# Revit family: 879-002X7X-001-DN65-150
name_source: partatom
category: Pipe Accessories
units: mm (PartAtom-declared; Revit-internal decimal feet)

## family parameters
Always vertical = Yes
Cut with Voids When Loaded = No
Part Type = Valve - Breaks Into
Round Connector Dimension = Use Diameter
Shared = No
Work Plane-Based = No

## types (32) — shared parameters
879-0065-00-14400207299 = DN65_PN10/16
879-0065-00-144002072A0 = DN65_PN10/16
879-0065-00-14400217299 = DN65_PN10/16
879-0065-00-144002172A0 = DN65_PN10/16
879-0065-00-14400227299 = DN65_PN10/16
879-0065-00-144002272A0 = DN65_PN10/16
879-0080-00-14400207299 = DN80_PN10/16
879-0080-00-144002072A0 = DN80_PN10/16
879-0080-00-14400217299 = DN80_PN10/16
879-0080-00-144002172A0 = DN80_PN10/16
879-0080-00-14400227299 = DN80_PN10/16
879-0080-00-144002272A0 = DN80_PN10/16
879-0100-00-14400207299 = DN100_PN10/16
879-0100-00-144002072A0 = DN100_PN10/16
879-0100-00-14400217299 = DN100_PN10/16
879-0100-00-144002172A0 = DN100_PN10/16
879-0100-00-14400227299 = DN100_PN10/16
879-0100-00-144002272A0 = DN100_PN10/16
879-0125-00-14400207299 = DN125_PN10/16
879-0125-00-144002072A0 = DN125_PN10/16
879-0125-00-14400217299 = DN125_PN10/16
879-0125-00-144002172A0 = DN125_PN10/16
879-0125-00-14400227299 = DN125_PN10/16
879-0125-00-144002272A0 = DN125_PN10/16
879-0150-00-14400207299 = DN150_PN10/16
879-0150-00-144002072A0 = DN150_PN10/16
879-0150-00-14400217299 = DN150_PN10/16
879-0150-00-144002172A0 = DN150_PN10/16
879-0150-00-14400227299 = DN150_PN10/16
879-0150-00-144002272A0 = DN150_PN10/16
879-0150-00-14400237299 = DN150_PN10/16
879-0150-00-144002372A0 = DN150_PN10/16
Body_wall_thickness = 10 mm  [stored 0.0328084 ft]
Description_ = AVK CONST. FLOW/PRESS. RED. CONTROL VALVE
Flange_thickness = 19 mm
Search_Table = 879-002X7X-001-DN65-150
URL product pages = https://www.avkvalves.com

## per-type parameters (varying)
- 879-0065-00-14400207299_DN65_PN10/16: A=121.75 mm; Body_Collar_Dia=30.21 mm; Body_Collar_Dia_2=14.5 mm; Body_Flange_Dia=76.32 mm; Body_Flange_Dia_2=78.38 mm; Body_Height_1=72.5 mm; Body_Height_2=36.25 mm; Body_Height_3=58 mm; Body_Height_4=51.25 mm; Body_Top_Dia=9.06 mm; Body_Top_Dia_2=7.55 mm; Body_With_Dia=64.44 mm; Body_With_Dia_2=64.44 mm; Bolt_support=170.59 mm; Bolt_support_2=85.29 mm; Bolt_support_Dia=12 mm  [stored 0.0393701 ft]; Bolt_support_lenght=52.5 mm; Bolt_support_lenght_2=62.5 mm; Bottom_profile=16.25 mm  [stored 0.0533136 ft]; D1=59 mm; DN=65 mm; FOD=92.5 mm; Fillet_Length=6 mm  [stored 0.019685 ft]; H3=485 mm; ID=32.5 mm; L=290 mm; L1=307 mm; L_Ref=298.5 mm; L_ref_2=126 mm; PG_Dia=40 mm; PG_Ref=48.33 mm; PG_depth=8.4 mm  [stored 0.0275591 ft]; PG_ref=42.5 mm; Pilot_Dia_1=17.5 mm  [stored 0.0574147 ft]; Pilot_Dia_1_Ref=21 mm; Pilot_Dia_1_Ref_2=42 mm; Pilot_Dia_2=43.75 mm; Pilot_Dia_3=11.67 mm; Pilot_Dia_4=5.83 mm; Pilot_Dia_5=3.89 mm; Pilot_top_1=297.13 mm; Pilot_top_ref=95.38 mm; Profile1_Height=152 mm; Profile1_Length=25 mm; Profile1_Length_2=16.67 mm; Profile_Dia=6 mm  [stored 0.019685 ft]; Profile_Dia_2=6 mm  [stored 0.019685 ft]; Profile_Dia_3=12 mm  [stored 0.0393701 ft]; Top_Profile=102.35 mm; Top_Profile_Ref=107.35 mm; Top_Ref=201.75 mm; Top_Ref_2=249.44 mm; W=255 mm; W_Ref=211.25 mm
- 879-0065-00-144002072A0_DN65_PN10/16: A=121.75 mm; Body_Collar_Dia=30.21 mm; Body_Collar_Dia_2=14.5 mm; Body_Flange_Dia=76.32 mm; Body_Flange_Dia_2=78.38 mm; Body_Height_1=72.5 mm; Body_Height_2=36.25 mm; Body_Height_3=72.5 mm; Body_Height_4=51.25 mm; Body_Top_Dia=9.06 mm; Body_Top_Dia_2=7.55 mm; Body_With_Dia=64.44 mm; Body_With_Dia_2=64.44 mm; Bolt_support=170.59 mm; Bolt_support_2=85.29 mm; Bolt_support_Dia=12 mm  [stored 0.0393701 ft]; Bolt_support_lenght=52.55 mm; Bolt_support_lenght_2=62.55 mm; Bottom_profile=16.28 mm; D1=59 mm; DN=65.1 mm; FOD=92.5 mm; Fillet_Length=6 mm  [stored 0.019685 ft]; H3=485 mm; ID=32.55 mm; L=290 mm; L1=307 mm; L_Ref=298.5 mm; L_ref_2=126 mm; PG_Dia=40 mm; PG_Ref=48.33 mm; PG_depth=8.4 mm  [stored 0.0275591 ft]; PG_ref=42.55 mm; Pilot_Dia_1=17.5 mm  [stored 0.0574147 ft]; Pilot_Dia_1_Ref=21 mm; Pilot_Dia_1_Ref_2=42 mm; Pilot_Dia_2=43.75 mm; Pilot_Dia_3=11.67 mm; Pilot_Dia_4=5.83 mm; Pilot_Dia_5=3.89 mm; Pilot_top_1=304.38 mm; Pilot_top_ref=88.13 mm; Profile1_Height=170 mm; Profile1_Length=25 mm; Profile1_Length_2=16.67 mm; Profile_Dia=6 mm  [stored 0.019685 ft]; Profile_Dia_2=6 mm  [stored 0.019685 ft]; Profile_Dia_3=12 mm  [stored 0.0393701 ft]; Top_Profile=102.35 mm; Top_Profile_Ref=107.35 mm; Top_Ref=216.25 mm; Top_Ref_2=260.31 mm; W=255 mm; W_Ref=211.25 mm
- 879-0065-00-14400217299_DN65_PN10/16: A=121.75 mm; Body_Collar_Dia=30.21 mm; Body_Collar_Dia_2=14.5 mm; Body_Flange_Dia=76.32 mm; Body_Flange_Dia_2=78.38 mm; Body_Height_1=72.5 mm; Body_Height_2=36.25 mm; Body_Height_3=58 mm; Body_Height_4=51.25 mm; Body_Top_Dia=9.06 mm; Body_Top_Dia_2=7.55 mm; Body_With_Dia=64.44 mm; Body_With_Dia_2=64.44 mm; Bolt_support=170.59 mm; Bolt_support_2=85.29 mm; Bolt_support_Dia=12 mm  [stored 0.0393701 ft]; Bolt_support_lenght=52.6 mm; Bolt_support_lenght_2=62.6 mm; Bottom_profile=16.3 mm; D1=59 mm; DN=65.2 mm; FOD=92.5 mm; Fillet_Length=6 mm  [stored 0.019685 ft]; H3=485 mm; ID=32.6 mm; L=290 mm; L1=307 mm; L_Ref=298.5 mm; L_ref_2=126 mm; PG_Dia=40 mm; PG_Ref=48.33 mm; PG_depth=8.4 mm  [stored 0.0275591 ft]; PG_ref=42.6 mm; Pilot_Dia_1=17.5 mm  [stored 0.0574147 ft]; Pilot_Dia_1_Ref=21 mm; Pilot_Dia_1_Ref_2=42 mm; Pilot_Dia_2=43.75 mm; Pilot_Dia_3=11.67 mm; Pilot_Dia_4=5.83 mm; Pilot_Dia_5=3.89 mm; Pilot_top_1=297.13 mm; Pilot_top_ref=95.38 mm; Profile1_Height=152 mm; Profile1_Length=25 mm; Profile1_Length_2=16.67 mm; Profile_Dia=6 mm  [stored 0.019685 ft]; Profile_Dia_2=6 mm  [stored 0.019685 ft]; Profile_Dia_3=12 mm  [stored 0.0393701 ft]; Top_Profile=102.35 mm; Top_Profile_Ref=107.35 mm; Top_Ref=201.75 mm; Top_Ref_2=249.44 mm; W=255 mm; W_Ref=211.25 mm
- 879-0065-00-144002172A0_DN65_PN10/16: A=121.75 mm; Body_Collar_Dia=30.21 mm; Body_Collar_Dia_2=14.5 mm; Body_Flange_Dia=76.32 mm; Body_Flange_Dia_2=78.38 mm; Body_Height_1=72.5 mm; Body_Height_2=36.25 mm; Body_Height_3=72.5 mm; Body_Height_4=51.25 mm; Body_Top_Dia=9.06 mm; Body_Top_Dia_2=7.55 mm; Body_With_Dia=64.44 mm; Body_With_Dia_2=64.44 mm; Bolt_support=170.59 mm; Bolt_support_2=85.29 mm; Bolt_support_Dia=12 mm  [stored 0.0393701 ft]; Bolt_support_lenght=52.65 mm; Bolt_support_lenght_2=62.65 mm; Bottom_profile=16.33 mm; D1=59 mm; DN=65.3 mm; FOD=92.5 mm; Fillet_Length=6 mm  [stored 0.019685 ft]; H3=485 mm; ID=32.65 mm; L=290 mm; L1=307 mm; L_Ref=298.5 mm; L_ref_2=126 mm; PG_Dia=40 mm; PG_Ref=48.33 mm; PG_depth=8.4 mm  [stored 0.0275591 ft]; PG_ref=42.65 mm; Pilot_Dia_1=17.5 mm  [stored 0.0574147 ft]; Pilot_Dia_1_Ref=21 mm; Pilot_Dia_1_Ref_2=42 mm; Pilot_Dia_2=43.75 mm; Pilot_Dia_3=11.67 mm; Pilot_Dia_4=5.83 mm; Pilot_Dia_5=3.89 mm; Pilot_top_1=304.38 mm; Pilot_top_ref=88.13 mm; Profile1_Height=170 mm; Profile1_Length=25 mm; Profile1_Length_2=16.67 mm; Profile_Dia=6 mm  [stored 0.019685 ft]; Profile_Dia_2=6 mm  [stored 0.019685 ft]; Profile_Dia_3=12 mm  [stored 0.0393701 ft]; Top_Profile=102.35 mm; Top_Profile_Ref=107.35 mm; Top_Ref=216.25 mm; Top_Ref_2=260.31 mm; W=255 mm; W_Ref=211.25 mm
- 879-0065-00-14400227299_DN65_PN10/16: A=121.75 mm; Body_Collar_Dia=30.21 mm; Body_Collar_Dia_2=14.5 mm; Body_Flange_Dia=76.32 mm; Body_Flange_Dia_2=78.38 mm; Body_Height_1=72.5 mm; Body_Height_2=36.25 mm; Body_Height_3=58 mm; Body_Height_4=51.25 mm; Body_Top_Dia=9.06 mm; Body_Top_Dia_2=7.55 mm; Body_With_Dia=64.44 mm; Body_With_Dia_2=64.44 mm; Bolt_support=170.59 mm; Bolt_support_2=85.29 mm; Bolt_support_Dia=12 mm  [stored 0.0393701 ft]; Bolt_support_lenght=52.7 mm; Bolt_support_lenght_2=62.7 mm; Bottom_profile=16.35 mm  [stored 0.0536417 ft]; D1=59 mm; DN=65.4 mm; FOD=92.5 mm; Fillet_Length=6 mm  [stored 0.019685 ft]; H3=485 mm; ID=32.7 mm; L=290 mm; L1=307 mm; L_Ref=298.5 mm; L_ref_2=126 mm; PG_Dia=40 mm; PG_Ref=48.33 mm; PG_depth=8.4 mm  [stored 0.0275591 ft]; PG_ref=42.7 mm; Pilot_Dia_1=17.5 mm  [stored 0.0574147 ft]; Pilot_Dia_1_Ref=21 mm; Pilot_Dia_1_Ref_2=42 mm; Pilot_Dia_2=43.75 mm; Pilot_Dia_3=11.67 mm; Pilot_Dia_4=5.83 mm; Pilot_Dia_5=3.89 mm; Pilot_top_1=297.13 mm; Pilot_top_ref=95.38 mm; Profile1_Height=152 mm; Profile1_Length=25 mm; Profile1_Length_2=16.67 mm; Profile_Dia=6 mm  [stored 0.019685 ft]; Profile_Dia_2=6 mm  [stored 0.019685 ft]; Profile_Dia_3=12 mm  [stored 0.0393701 ft]; Top_Profile=102.35 mm; Top_Profile_Ref=107.35 mm; Top_Ref=201.75 mm; Top_Ref_2=249.44 mm; W=255 mm; W_Ref=211.25 mm
- 879-0065-00-144002272A0_DN65_PN10/16: A=121.75 mm; Body_Collar_Dia=30.21 mm; Body_Collar_Dia_2=14.5 mm; Body_Flange_Dia=76.32 mm; Body_Flange_Dia_2=78.38 mm; Body_Height_1=72.5 mm; Body_Height_2=36.25 mm; Body_Height_3=72.5 mm; Body_Height_4=51.25 mm; Body_Top_Dia=9.06 mm; Body_Top_Dia_2=7.55 mm; Body_With_Dia=64.44 mm; Body_With_Dia_2=64.44 mm; Bolt_support=170.59 mm; Bolt_support_2=85.29 mm; Bolt_support_Dia=12 mm  [stored 0.0393701 ft]; Bolt_support_lenght=52.75 mm; Bolt_support_lenght_2=62.75 mm; Bottom_profile=16.38 mm; D1=59 mm; DN=65.5 mm; FOD=92.5 mm; Fillet_Length=6 mm  [stored 0.019685 ft]; H3=485 mm; ID=32.75 mm; L=290 mm; L1=307 mm; L_Ref=298.5 mm; L_ref_2=126 mm; PG_Dia=40 mm; PG_Ref=48.33 mm; PG_depth=8.4 mm  [stored 0.0275591 ft]; PG_ref=42.75 mm; Pilot_Dia_1=17.5 mm  [stored 0.0574147 ft]; Pilot_Dia_1_Ref=21 mm; Pilot_Dia_1_Ref_2=42 mm; Pilot_Dia_2=43.75 mm; Pilot_Dia_3=11.67 mm; Pilot_Dia_4=5.83 mm; Pilot_Dia_5=3.89 mm; Pilot_top_1=304.38 mm; Pilot_top_ref=88.13 mm; Profile1_Height=170 mm; Profile1_Length=25 mm; Profile1_Length_2=16.67 mm; Profile_Dia=6 mm  [stored 0.019685 ft]; Profile_Dia_2=6 mm  [stored 0.019685 ft]; Profile_Dia_3=12 mm  [stored 0.0393701 ft]; Top_Profile=102.35 mm; Top_Profile_Ref=107.35 mm; Top_Ref=216.25 mm; Top_Ref_2=260.31 mm; W=255 mm; W_Ref=211.25 mm
- 879-0100-00-14400207299_DN100_PN10/16: A=128 mm; Body_Collar_Dia=36.46 mm; Body_Collar_Dia_2=17.5 mm  [stored 0.0574147 ft]; Body_Flange_Dia=92.11 mm; Body_Flange_Dia_2=94.59 mm; Body_Height_1=87.5 mm; Body_Height_2=43.75 mm; Body_Height_3=58.5 mm; Body_Height_4=58.75 mm; Body_Top_Dia=10.94 mm; Body_Top_Dia_2=9.11 mm; Body_With_Dia=77.78 mm; Body_With_Dia_2=77.78 mm; Bolt_support=205.88 mm; Bolt_support_2=102.94 mm; Bolt_support_Dia=12 mm  [stored 0.0393701 ft]; Bolt_support_lenght=70 mm; Bolt_support_lenght_2=80 mm; Bottom_profile=25 mm; D1=78 mm; DN=100 mm; FOD=110 mm; Fillet_Length=6 mm  [stored 0.019685 ft]; H3=520 mm; ID=50 mm; L=350 mm; L1=367 mm; L_Ref=358.5 mm; L_ref_2=156 mm; PG_Dia=40 mm; PG_Ref=58.33 mm; PG_depth=8.4 mm  [stored 0.0275591 ft]; PG_ref=60 mm; Pilot_Dia_1=22 mm; Pilot_Dia_1_Ref=26.4 mm; Pilot_Dia_1_Ref_2=52.8 mm; Pilot_Dia_2=55 mm; Pilot_Dia_3=14.67 mm; Pilot_Dia_4=7.33 mm; Pilot_Dia_5=4.89 mm; Pilot_top_1=317.38 mm; Pilot_top_ref=92.63 mm; Profile1_Height=185 mm; Profile1_Length=29.73 mm; Profile1_Length_2=19.82 mm; Profile_Dia=6 mm  [stored 0.019685 ft]; Profile_Dia_2=6 mm  [stored 0.019685 ft]; Profile_Dia_3=12 mm  [stored 0.0393701 ft]; Top_Profile=123.53 mm; Top_Profile_Ref=128.53 mm; Top_Ref=224.75 mm; Top_Ref_2=271.06 mm; W=290 mm; W_Ref=235 mm
- 879-0100-00-144002072A0_DN100_PN10/16: A=128 mm; Body_Collar_Dia=36.46 mm; Body_Collar_Dia_2=17.5 mm  [stored 0.0574147 ft]; Body_Flange_Dia=92.11 mm; Body_Flange_Dia_2=94.59 mm; Body_Height_1=87.5 mm; Body_Height_2=43.75 mm; Body_Height_3=70 mm; Body_Height_4=58.75 mm; Body_Top_Dia=10.94 mm; Body_Top_Dia_2=9.11 mm; Body_With_Dia=77.78 mm; Body_With_Dia_2=77.78 mm; Bolt_support=205.88 mm; Bolt_support_2=102.94 mm; Bolt_support_Dia=12 mm  [stored 0.0393701 ft]; Bolt_support_lenght=70.05 mm; Bolt_support_lenght_2=80.05 mm; Bottom_profile=25.03 mm; D1=78 mm; DN=100.1 mm; FOD=110 mm; Fillet_Length=6 mm  [stored 0.019685 ft]; H3=520 mm; ID=50.05 mm; L=350 mm; L1=367 mm; L_Ref=358.5 mm; L_ref_2=156 mm; PG_Dia=40 mm; PG_Ref=58.33 mm; PG_depth=8.4 mm  [stored 0.0275591 ft]; PG_ref=60.05 mm; Pilot_Dia_1=22 mm; Pilot_Dia_1_Ref=26.4 mm; Pilot_Dia_1_Ref_2=52.8 mm; Pilot_Dia_2=55 mm; Pilot_Dia_3=14.67 mm; Pilot_Dia_4=7.33 mm; Pilot_Dia_5=4.89 mm; Pilot_top_1=323.13 mm; Pilot_top_ref=86.88 mm; Profile1_Height=176 mm; Profile1_Length=29.73 mm; Profile1_Length_2=19.82 mm; Profile_Dia=6 mm  [stored 0.019685 ft]; Profile_Dia_2=6 mm  [stored 0.019685 ft]; Profile_Dia_3=12 mm  [stored 0.0393701 ft]; Top_Profile=123.53 mm; Top_Profile_Ref=128.53 mm; Top_Ref=236.25 mm; Top_Ref_2=279.69 mm; W=290 mm; W_Ref=235 mm
- 879-0100-00-14400217299_DN100_PN10/16: A=128 mm; Body_Collar_Dia=36.46 mm; Body_Collar_Dia_2=17.5 mm  [stored 0.0574147 ft]; Body_Flange_Dia=92.11 mm; Body_Flange_Dia_2=94.59 mm; Body_Height_1=87.5 mm; Body_Height_2=43.75 mm; Body_Height_3=58.5 mm; Body_Height_4=58.75 mm; Body_Top_Dia=10.94 mm; Body_Top_Dia_2=9.11 mm; Body_With_Dia=77.78 mm; Body_With_Dia_2=77.78 mm; Bolt_support=205.88 mm; Bolt_support_2=102.94 mm; Bolt_support_Dia=12 mm  [stored 0.0393701 ft]; Bolt_support_lenght=70.1 mm; Bolt_support_lenght_2=80.1 mm; Bottom_profile=25.05 mm; D1=78 mm; DN=100.2 mm; FOD=110 mm; Fillet_Length=6 mm  [stored 0.019685 ft]; H3=520 mm; ID=50.1 mm; L=350 mm; L1=367 mm; L_Ref=358.5 mm; L_ref_2=156 mm; PG_Dia=40 mm; PG_Ref=58.33 mm; PG_depth=8.4 mm  [stored 0.0275591 ft]; PG_ref=60.1 mm; Pilot_Dia_1=22 mm; Pilot_Dia_1_Ref=26.4 mm; Pilot_Dia_1_Ref_2=52.8 mm; Pilot_Dia_2=55 mm; Pilot_Dia_3=14.67 mm; Pilot_Dia_4=7.33 mm; Pilot_Dia_5=4.89 mm; Pilot_top_1=317.38 mm; Pilot_top_ref=92.63 mm; Profile1_Height=185 mm; Profile1_Length=29.73 mm; Profile1_Length_2=19.82 mm; Profile_Dia=6 mm  [stored 0.019685 ft]; Profile_Dia_2=6 mm  [stored 0.019685 ft]; Profile_Dia_3=12 mm  [stored 0.0393701 ft]; Top_Profile=123.53 mm; Top_Profile_Ref=128.53 mm; Top_Ref=224.75 mm; Top_Ref_2=271.06 mm; W=290 mm; W_Ref=235 mm
- 879-0100-00-144002172A0_DN100_PN10/16: A=128 mm; Body_Collar_Dia=36.46 mm; Body_Collar_Dia_2=17.5 mm  [stored 0.0574147 ft]; Body_Flange_Dia=92.11 mm; Body_Flange_Dia_2=94.59 mm; Body_Height_1=87.5 mm; Body_Height_2=43.75 mm; Body_Height_3=70 mm; Body_Height_4=58.75 mm; Body_Top_Dia=10.94 mm; Body_Top_Dia_2=9.11 mm; Body_With_Dia=77.78 mm; Body_With_Dia_2=77.78 mm; Bolt_support=205.88 mm; Bolt_support_2=102.94 mm; Bolt_support_Dia=12 mm  [stored 0.0393701 ft]; Bolt_support_lenght=70.15 mm; Bolt_support_lenght_2=80.15 mm; Bottom_profile=25.08 mm; D1=78 mm; DN=100.3 mm; FOD=110 mm; Fillet_Length=6 mm  [stored 0.019685 ft]; H3=520 mm; ID=50.15 mm; L=350 mm; L1=367 mm; L_Ref=358.5 mm; L_ref_2=156 mm; PG_Dia=40 mm; PG_Ref=58.33 mm; PG_depth=8.4 mm  [stored 0.0275591 ft]; PG_ref=60.15 mm; Pilot_Dia_1=22 mm; Pilot_Dia_1_Ref=26.4 mm; Pilot_Dia_1_Ref_2=52.8 mm; Pilot_Dia_2=55 mm; Pilot_Dia_3=14.67 mm; Pilot_Dia_4=7.33 mm; Pilot_Dia_5=4.89 mm; Pilot_top_1=323.13 mm; Pilot_top_ref=86.88 mm; Profile1_Height=176 mm; Profile1_Length=29.73 mm; Profile1_Length_2=19.82 mm; Profile_Dia=6 mm  [stored 0.019685 ft]; Profile_Dia_2=6 mm  [stored 0.019685 ft]; Profile_Dia_3=12 mm  [stored 0.0393701 ft]; Top_Profile=123.53 mm; Top_Profile_Ref=128.53 mm; Top_Ref=236.25 mm; Top_Ref_2=279.69 mm; W=290 mm; W_Ref=235 mm
- 879-0100-00-14400227299_DN100_PN10/16: A=128 mm; Body_Collar_Dia=36.46 mm; Body_Collar_Dia_2=17.5 mm  [stored 0.0574147 ft]; Body_Flange_Dia=92.11 mm; Body_Flange_Dia_2=94.59 mm; Body_Height_1=87.5 mm; Body_Height_2=43.75 mm; Body_Height_3=58.5 mm; Body_Height_4=58.75 mm; Body_Top_Dia=10.94 mm; Body_Top_Dia_2=9.11 mm; Body_With_Dia=77.78 mm; Body_With_Dia_2=77.78 mm; Bolt_support=205.88 mm; Bolt_support_2=102.94 mm; Bolt_support_Dia=12 mm  [stored 0.0393701 ft]; Bolt_support_lenght=70.2 mm; Bolt_support_lenght_2=80.2 mm; Bottom_profile=25.1 mm; D1=78 mm; DN=100.4 mm; FOD=110 mm; Fillet_Length=6 mm  [stored 0.019685 ft]; H3=520 mm; ID=50.2 mm; L=350 mm; L1=367 mm; L_Ref=358.5 mm; L_ref_2=156 mm; PG_Dia=40 mm; PG_Ref=58.33 mm; PG_depth=8.4 mm  [stored 0.0275591 ft]; PG_ref=60.2 mm; Pilot_Dia_1=22 mm; Pilot_Dia_1_Ref=26.4 mm; Pilot_Dia_1_Ref_2=52.8 mm; Pilot_Dia_2=55 mm; Pilot_Dia_3=14.67 mm; Pilot_Dia_4=7.33 mm; Pilot_Dia_5=4.89 mm; Pilot_top_1=317.38 mm; Pilot_top_ref=92.63 mm; Profile1_Height=185 mm; Profile1_Length=29.73 mm; Profile1_Length_2=19.82 mm; Profile_Dia=6 mm  [stored 0.019685 ft]; Profile_Dia_2=6 mm  [stored 0.019685 ft]; Profile_Dia_3=12 mm  [stored 0.0393701 ft]; Top_Profile=123.53 mm; Top_Profile_Ref=128.53 mm; Top_Ref=224.75 mm; Top_Ref_2=271.06 mm; W=290 mm; W_Ref=235 mm
- 879-0100-00-144002272A0_DN100_PN10/16: A=128 mm; Body_Collar_Dia=36.46 mm; Body_Collar_Dia_2=17.5 mm  [stored 0.0574147 ft]; Body_Flange_Dia=92.11 mm; Body_Flange_Dia_2=94.59 mm; Body_Height_1=87.5 mm; Body_Height_2=43.75 mm; Body_Height_3=70 mm; Body_Height_4=58.75 mm; Body_Top_Dia=10.94 mm; Body_Top_Dia_2=9.11 mm; Body_With_Dia=77.78 mm; Body_With_Dia_2=77.78 mm; Bolt_support=205.88 mm; Bolt_support_2=102.94 mm; Bolt_support_Dia=12 mm  [stored 0.0393701 ft]; Bolt_support_lenght=70.25 mm; Bolt_support_lenght_2=80.25 mm; Bottom_profile=25.13 mm; D1=78 mm; DN=100.5 mm; FOD=110 mm; Fillet_Length=6 mm  [stored 0.019685 ft]; H3=520 mm; ID=50.25 mm; L=350 mm; L1=367 mm; L_Ref=358.5 mm; L_ref_2=156 mm; PG_Dia=40 mm; PG_Ref=58.33 mm; PG_depth=8.4 mm  [stored 0.0275591 ft]; PG_ref=60.25 mm; Pilot_Dia_1=22 mm; Pilot_Dia_1_Ref=26.4 mm; Pilot_Dia_1_Ref_2=52.8 mm; Pilot_Dia_2=55 mm; Pilot_Dia_3=14.67 mm; Pilot_Dia_4=7.33 mm; Pilot_Dia_5=4.89 mm; Pilot_top_1=323.13 mm; Pilot_top_ref=86.88 mm; Profile1_Height=176 mm; Profile1_Length=29.73 mm; Profile1_Length_2=19.82 mm; Profile_Dia=6 mm  [stored 0.019685 ft]; Profile_Dia_2=6 mm  [stored 0.019685 ft]; Profile_Dia_3=12 mm  [stored 0.0393701 ft]; Top_Profile=123.53 mm; Top_Profile_Ref=128.53 mm; Top_Ref=236.25 mm; Top_Ref_2=279.69 mm; W=290 mm; W_Ref=235 mm
- 879-0125-00-14400207299_DN125_PN10/16: A=119.25 mm; Body_Collar_Dia=41.67 mm; Body_Collar_Dia_2=20 mm; Body_Flange_Dia=105.26 mm; Body_Flange_Dia_2=108.11 mm; Body_Height_1=100 mm; Body_Height_2=50 mm; Body_Height_3=58.5 mm; Body_Height_4=65 mm; Body_Top_Dia=12.5 mm  [stored 0.0410105 ft]; Body_Top_Dia_2=10.42 mm; Body_With_Dia=88.89 mm; Body_With_Dia_2=88.89 mm; Bolt_support=235.29 mm; Bolt_support_2=117.65 mm; Bolt_support_Dia=12 mm  [stored 0.0393701 ft]; Bolt_support_lenght=82.5 mm; Bolt_support_lenght_2=92.5 mm; Bottom_profile=31.25 mm; D1=92 mm; DN=125 mm; FOD=125 mm; Fillet_Length=6 mm  [stored 0.019685 ft]; H3=540 mm; ID=62.5 mm; L=400 mm; L1=417 mm; L_Ref=408.5 mm; L_ref_2=181 mm; PG_Dia=40 mm; PG_Ref=66.67 mm; PG_depth=8.4 mm  [stored 0.0275591 ft]; PG_ref=72.5 mm; Pilot_Dia_1=27.5 mm; Pilot_Dia_1_Ref=33 mm; Pilot_Dia_1_Ref_2=66 mm; Pilot_Dia_2=68.75 mm; Pilot_Dia_3=18.33 mm; Pilot_Dia_4=9.17 mm; Pilot_Dia_5=6.11 mm; Pilot_top_1=329.25 mm; Pilot_top_ref=85.75 mm; Profile1_Height=205 mm; Profile1_Length=33.78 mm; Profile1_Length_2=22.52 mm; Profile_Dia=6 mm  [stored 0.019685 ft]; Profile_Dia_2=6 mm  [stored 0.019685 ft]; Profile_Dia_3=12 mm  [stored 0.0393701 ft]; Top_Profile=141.18 mm; Top_Profile_Ref=146.18 mm; Top_Ref=243.5 mm; Top_Ref_2=286.38 mm; W=310 mm; W_Ref=241.25 mm
- 879-0125-00-144002072A0_DN125_PN10/16: A=119.25 mm; Body_Collar_Dia=41.67 mm; Body_Collar_Dia_2=20 mm; Body_Flange_Dia=105.26 mm; Body_Flange_Dia_2=108.11 mm; Body_Height_1=100 mm; Body_Height_2=50 mm; Body_Height_3=70 mm; Body_Height_4=65 mm; Body_Top_Dia=12.5 mm  [stored 0.0410105 ft]; Body_Top_Dia_2=10.42 mm; Body_With_Dia=88.89 mm; Body_With_Dia_2=88.89 mm; Bolt_support=235.29 mm; Bolt_support_2=117.65 mm; Bolt_support_Dia=12 mm  [stored 0.0393701 ft]; Bolt_support_lenght=82.55 mm; Bolt_support_lenght_2=92.55 mm; Bottom_profile=31.28 mm; D1=92 mm; DN=125.1 mm; FOD=125 mm; Fillet_Length=6 mm  [stored 0.019685 ft]; H3=540 mm; ID=62.55 mm; L=400 mm; L1=417 mm; L_Ref=408.5 mm; L_ref_2=181 mm; PG_Dia=40 mm; PG_Ref=66.67 mm; PG_depth=8.4 mm  [stored 0.0275591 ft]; PG_ref=72.55 mm; Pilot_Dia_1=27.5 mm; Pilot_Dia_1_Ref=33 mm; Pilot_Dia_1_Ref_2=66 mm; Pilot_Dia_2=68.75 mm; Pilot_Dia_3=18.33 mm; Pilot_Dia_4=9.17 mm; Pilot_Dia_5=6.11 mm; Pilot_top_1=335 mm; Pilot_top_ref=80 mm; Profile1_Height=195 mm; Profile1_Length=33.78 mm; Profile1_Length_2=22.52 mm; Profile_Dia=6 mm  [stored 0.019685 ft]; Profile_Dia_2=6 mm  [stored 0.019685 ft]; Profile_Dia_3=12 mm  [stored 0.0393701 ft]; Top_Profile=141.18 mm; Top_Profile_Ref=146.18 mm; Top_Ref=255 mm; Top_Ref_2=295 mm; W=310 mm; W_Ref=241.25 mm
- 879-0125-00-14400217299_DN125_PN10/16: A=119.25 mm; Body_Collar_Dia=41.67 mm; Body_Collar_Dia_2=20 mm; Body_Flange_Dia=105.26 mm; Body_Flange_Dia_2=108.11 mm; Body_Height_1=100 mm; Body_Height_2=50 mm; Body_Height_3=58.5 mm; Body_Height_4=65 mm; Body_Top_Dia=12.5 mm  [stored 0.0410105 ft]; Body_Top_Dia_2=10.42 mm; Body_With_Dia=88.89 mm; Body_With_Dia_2=88.89 mm; Bolt_support=235.29 mm; Bolt_support_2=117.65 mm; Bolt_support_Dia=12 mm  [stored 0.0393701 ft]; Bolt_support_lenght=82.6 mm; Bolt_support_lenght_2=92.6 mm; Bottom_profile=31.3 mm; D1=92 mm; DN=125.2 mm; FOD=125 mm; Fillet_Length=6 mm  [stored 0.019685 ft]; H3=540 mm; ID=62.6 mm; L=400 mm; L1=417 mm; L_Ref=408.5 mm; L_ref_2=181 mm; PG_Dia=40 mm; PG_Ref=66.67 mm; PG_depth=8.4 mm  [stored 0.0275591 ft]; PG_ref=72.6 mm; Pilot_Dia_1=27.5 mm; Pilot_Dia_1_Ref=33 mm; Pilot_Dia_1_Ref_2=66 mm; Pilot_Dia_2=68.75 mm; Pilot_Dia_3=18.33 mm; Pilot_Dia_4=9.17 mm; Pilot_Dia_5=6.11 mm; Pilot_top_1=329.25 mm; Pilot_top_ref=85.75 mm; Profile1_Height=205 mm; Profile1_Length=33.78 mm; Profile1_Length_2=22.52 mm; Profile_Dia=6 mm  [stored 0.019685 ft]; Profile_Dia_2=6 mm  [stored 0.019685 ft]; Profile_Dia_3=12 mm  [stored 0.0393701 ft]; Top_Profile=141.18 mm; Top_Profile_Ref=146.18 mm; Top_Ref=243.5 mm; Top_Ref_2=286.38 mm; W=310 mm; W_Ref=241.25 mm
- 879-0125-00-144002172A0_DN125_PN10/16: A=119.25 mm; Body_Collar_Dia=41.67 mm; Body_Collar_Dia_2=20 mm; Body_Flange_Dia=105.26 mm; Body_Flange_Dia_2=108.11 mm; Body_Height_1=100 mm; Body_Height_2=50 mm; Body_Height_3=70 mm; Body_Height_4=65 mm; Body_Top_Dia=12.5 mm  [stored 0.0410105 ft]; Body_Top_Dia_2=10.42 mm; Body_With_Dia=88.89 mm; Body_With_Dia_2=88.89 mm; Bolt_support=235.29 mm; Bolt_support_2=117.65 mm; Bolt_support_Dia=12 mm  [stored 0.0393701 ft]; Bolt_support_lenght=82.65 mm; Bolt_support_lenght_2=92.65 mm; Bottom_profile=31.33 mm; D1=92 mm; DN=125.3 mm; FOD=125 mm; Fillet_Length=6 mm  [stored 0.019685 ft]; H3=540 mm; ID=62.65 mm; L=400 mm; L1=417 mm; L_Ref=408.5 mm; L_ref_2=181 mm; PG_Dia=40 mm; PG_Ref=66.67 mm; PG_depth=8.4 mm  [stored 0.0275591 ft]; PG_ref=72.65 mm; Pilot_Dia_1=27.5 mm; Pilot_Dia_1_Ref=33 mm; Pilot_Dia_1_Ref_2=66 mm; Pilot_Dia_2=68.75 mm; Pilot_Dia_3=18.33 mm; Pilot_Dia_4=9.17 mm; Pilot_Dia_5=6.11 mm; Pilot_top_1=335 mm; Pilot_top_ref=80 mm; Profile1_Height=195 mm; Profile1_Length=33.78 mm; Profile1_Length_2=22.52 mm; Profile_Dia=6 mm  [stored 0.019685 ft]; Profile_Dia_2=6 mm  [stored 0.019685 ft]; Profile_Dia_3=12 mm  [stored 0.0393701 ft]; Top_Profile=141.18 mm; Top_Profile_Ref=146.18 mm; Top_Ref=255 mm; Top_Ref_2=295 mm; W=310 mm; W_Ref=241.25 mm
- 879-0125-00-14400227299_DN125_PN10/16: A=119.25 mm; Body_Collar_Dia=41.67 mm; Body_Collar_Dia_2=20 mm; Body_Flange_Dia=105.26 mm; Body_Flange_Dia_2=108.11 mm; Body_Height_1=100 mm; Body_Height_2=50 mm; Body_Height_3=58.5 mm; Body_Height_4=65 mm; Body_Top_Dia=12.5 mm  [stored 0.0410105 ft]; Body_Top_Dia_2=10.42 mm; Body_With_Dia=88.89 mm; Body_With_Dia_2=88.89 mm; Bolt_support=235.29 mm; Bolt_support_2=117.65 mm; Bolt_support_Dia=12 mm  [stored 0.0393701 ft]; Bolt_support_lenght=82.7 mm; Bolt_support_lenght_2=92.7 mm; Bottom_profile=31.35 mm; D1=92 mm; DN=125.4 mm; FOD=125 mm; Fillet_Length=6 mm  [stored 0.019685 ft]; H3=540 mm; ID=62.7 mm; L=400 mm; L1=417 mm; L_Ref=408.5 mm; L_ref_2=181 mm; PG_Dia=40 mm; PG_Ref=66.67 mm; PG_depth=8.4 mm  [stored 0.0275591 ft]; PG_ref=72.7 mm; Pilot_Dia_1=27.5 mm; Pilot_Dia_1_Ref=33 mm; Pilot_Dia_1_Ref_2=66 mm; Pilot_Dia_2=68.75 mm; Pilot_Dia_3=18.33 mm; Pilot_Dia_4=9.17 mm; Pilot_Dia_5=6.11 mm; Pilot_top_1=329.25 mm; Pilot_top_ref=85.75 mm; Profile1_Height=205 mm; Profile1_Length=33.78 mm; Profile1_Length_2=22.52 mm; Profile_Dia=6 mm  [stored 0.019685 ft]; Profile_Dia_2=6 mm  [stored 0.019685 ft]; Profile_Dia_3=12 mm  [stored 0.0393701 ft]; Top_Profile=141.18 mm; Top_Profile_Ref=146.18 mm; Top_Ref=243.5 mm; Top_Ref_2=286.38 mm; W=310 mm; W_Ref=241.25 mm
- 879-0125-00-144002272A0_DN125_PN10/16: A=119.25 mm; Body_Collar_Dia=41.67 mm; Body_Collar_Dia_2=20 mm; Body_Flange_Dia=105.26 mm; Body_Flange_Dia_2=108.11 mm; Body_Height_1=100 mm; Body_Height_2=50 mm; Body_Height_3=70 mm; Body_Height_4=65 mm; Body_Top_Dia=12.5 mm  [stored 0.0410105 ft]; Body_Top_Dia_2=10.42 mm; Body_With_Dia=88.89 mm; Body_With_Dia_2=88.89 mm; Bolt_support=235.29 mm; Bolt_support_2=117.65 mm; Bolt_support_Dia=12 mm  [stored 0.0393701 ft]; Bolt_support_lenght=82.75 mm; Bolt_support_lenght_2=92.75 mm; Bottom_profile=31.38 mm; D1=92 mm; DN=125.5 mm; FOD=125 mm; Fillet_Length=6 mm  [stored 0.019685 ft]; H3=540 mm; ID=62.75 mm; L=400 mm; L1=417 mm; L_Ref=408.5 mm; L_ref_2=181 mm; PG_Dia=40 mm; PG_Ref=66.67 mm; PG_depth=8.4 mm  [stored 0.0275591 ft]; PG_ref=72.75 mm; Pilot_Dia_1=27.5 mm; Pilot_Dia_1_Ref=33 mm; Pilot_Dia_1_Ref_2=66 mm; Pilot_Dia_2=68.75 mm; Pilot_Dia_3=18.33 mm; Pilot_Dia_4=9.17 mm; Pilot_Dia_5=6.11 mm; Pilot_top_1=335 mm; Pilot_top_ref=80 mm; Profile1_Height=195 mm; Profile1_Length=33.78 mm; Profile1_Length_2=22.52 mm; Profile_Dia=6 mm  [stored 0.019685 ft]; Profile_Dia_2=6 mm  [stored 0.019685 ft]; Profile_Dia_3=12 mm  [stored 0.0393701 ft]; Top_Profile=141.18 mm; Top_Profile_Ref=146.18 mm; Top_Ref=255 mm; Top_Ref_2=295 mm; W=310 mm; W_Ref=241.25 mm
- 879-0150-00-14400207299_DN150_PN10/16: A=124 mm; Body_Collar_Dia=50 mm; Body_Collar_Dia_2=24 mm; Body_Flange_Dia=126.32 mm; Body_Flange_Dia_2=129.73 mm; Body_Height_1=120 mm; Body_Height_2=60 mm; Body_Height_3=60 mm; Body_Height_4=75 mm; Body_Top_Dia=15 mm  [stored 0.0492126 ft]; Body_Top_Dia_2=12.5 mm  [stored 0.0410105 ft]; Body_With_Dia=106.67 mm; Body_With_Dia_2=106.67 mm; Bolt_support=282.35 mm; Bolt_support_2=141.18 mm; Bolt_support_Dia=16 mm  [stored 0.0524934 ft]; Bolt_support_lenght=95 mm; Bolt_support_lenght_2=105 mm; Bottom_profile=37.5 mm; D1=105.5 mm; DN=150 mm; FOD=142.5 mm; Fillet_Length=8 mm  [stored 0.0262467 ft]; H3=525 mm; ID=75 mm; L=480 mm; L1=497 mm; L_Ref=488.5 mm; L_ref_2=221 mm; PG_Dia=80 mm; PG_Ref=80 mm; PG_depth=11.2 mm  [stored 0.0367454 ft]; PG_ref=85 mm; Pilot_Dia_1=31 mm; Pilot_Dia_1_Ref=37.2 mm; Pilot_Dia_1_Ref_2=74.4 mm; Pilot_Dia_2=77.5 mm; Pilot_Dia_3=20.67 mm; Pilot_Dia_4=10.33 mm; Pilot_Dia_5=6.89 mm; Pilot_top_1=328.75 mm; Pilot_top_ref=53.75 mm; Profile1_Height=230 mm; Profile1_Length=38.51 mm; Profile1_Length_2=25.68 mm; Profile_Dia=8 mm  [stored 0.0262467 ft]; Profile_Dia_2=8 mm  [stored 0.0262467 ft]; Profile_Dia_3=16 mm  [stored 0.0524934 ft]; Top_Profile=169.41 mm; Top_Profile_Ref=174.41 mm; Top_Ref=275 mm; Top_Ref_2=301.88 mm; W=340 mm; W_Ref=262.5 mm
- 879-0150-00-144002072A0_DN150_PN10/16: A=124 mm; Body_Collar_Dia=50 mm; Body_Collar_Dia_2=24 mm; Body_Flange_Dia=126.32 mm; Body_Flange_Dia_2=129.73 mm; Body_Height_1=120 mm; Body_Height_2=60 mm; Body_Height_3=68 mm; Body_Height_4=75 mm; Body_Top_Dia=15 mm  [stored 0.0492126 ft]; Body_Top_Dia_2=12.5 mm  [stored 0.0410105 ft]; Body_With_Dia=106.67 mm; Body_With_Dia_2=106.67 mm; Bolt_support=282.35 mm; Bolt_support_2=141.18 mm; Bolt_support_Dia=16 mm  [stored 0.0524934 ft]; Bolt_support_lenght=95.05 mm; Bolt_support_lenght_2=105.05 mm; Bottom_profile=37.53 mm; D1=105.5 mm; DN=150.1 mm; FOD=142.5 mm; Fillet_Length=8 mm  [stored 0.0262467 ft]; H3=525 mm; ID=75.05 mm; L=480 mm; L1=497 mm; L_Ref=488.5 mm; L_ref_2=221 mm; PG_Dia=80 mm; PG_Ref=80 mm; PG_depth=11.2 mm  [stored 0.0367454 ft]; PG_ref=85.05 mm; Pilot_Dia_1=31 mm; Pilot_Dia_1_Ref=37.2 mm; Pilot_Dia_1_Ref_2=74.4 mm; Pilot_Dia_2=77.5 mm; Pilot_Dia_3=20.67 mm; Pilot_Dia_4=10.33 mm; Pilot_Dia_5=6.89 mm; Pilot_top_1=332.75 mm; Pilot_top_ref=49.75 mm; Profile1_Height=230 mm; Profile1_Length=38.51 mm; Profile1_Length_2=25.68 mm; Profile_Dia=8 mm  [stored 0.0262467 ft]; Profile_Dia_2=8 mm  [stored 0.0262467 ft]; Profile_Dia_3=16 mm  [stored 0.0524934 ft]; Top_Profile=169.41 mm; Top_Profile_Ref=174.41 mm; Top_Ref=283 mm; Top_Ref_2=307.88 mm; W=340 mm; W_Ref=262.5 mm
- 879-0150-00-14400217299_DN150_PN10/16: A=124 mm; Body_Collar_Dia=50 mm; Body_Collar_Dia_2=24 mm; Body_Flange_Dia=126.32 mm; Body_Flange_Dia_2=129.73 mm; Body_Height_1=120 mm; Body_Height_2=60 mm; Body_Height_3=60 mm; Body_Height_4=75 mm; Body_Top_Dia=15 mm  [stored 0.0492126 ft]; Body_Top_Dia_2=12.5 mm  [stored 0.0410105 ft]; Body_With_Dia=106.67 mm; Body_With_Dia_2=106.67 mm; Bolt_support=282.35 mm; Bolt_support_2=141.18 mm; Bolt_support_Dia=16 mm  [stored 0.0524934 ft]; Bolt_support_lenght=95.1 mm; Bolt_support_lenght_2=105.1 mm; Bottom_profile=37.55 mm; D1=105.5 mm; DN=150.2 mm; FOD=142.5 mm; Fillet_Length=8 mm  [stored 0.0262467 ft]; H3=525 mm; ID=75.1 mm; L=480 mm; L1=497 mm; L_Ref=488.5 mm; L_ref_2=221 mm; PG_Dia=80 mm; PG_Ref=80 mm; PG_depth=11.2 mm  [stored 0.0367454 ft]; PG_ref=85.1 mm; Pilot_Dia_1=31 mm; Pilot_Dia_1_Ref=37.2 mm; Pilot_Dia_1_Ref_2=74.4 mm; Pilot_Dia_2=77.5 mm; Pilot_Dia_3=20.67 mm; Pilot_Dia_4=10.33 mm; Pilot_Dia_5=6.89 mm; Pilot_top_1=328.75 mm; Pilot_top_ref=53.75 mm; Profile1_Height=230 mm; Profile1_Length=38.51 mm; Profile1_Length_2=25.68 mm; Profile_Dia=8 mm  [stored 0.0262467 ft]; Profile_Dia_2=8 mm  [stored 0.0262467 ft]; Profile_Dia_3=16 mm  [stored 0.0524934 ft]; Top_Profile=169.41 mm; Top_Profile_Ref=174.41 mm; Top_Ref=275 mm; Top_Ref_2=301.88 mm; W=340 mm; W_Ref=262.5 mm
- 879-0150-00-144002172A0_DN150_PN10/16: A=124 mm; Body_Collar_Dia=50 mm; Body_Collar_Dia_2=24 mm; Body_Flange_Dia=126.32 mm; Body_Flange_Dia_2=129.73 mm; Body_Height_1=120 mm; Body_Height_2=60 mm; Body_Height_3=68 mm; Body_Height_4=75 mm; Body_Top_Dia=15 mm  [stored 0.0492126 ft]; Body_Top_Dia_2=12.5 mm  [stored 0.0410105 ft]; Body_With_Dia=106.67 mm; Body_With_Dia_2=106.67 mm; Bolt_support=282.35 mm; Bolt_support_2=141.18 mm; Bolt_support_Dia=16 mm  [stored 0.0524934 ft]; Bolt_support_lenght=95.15 mm; Bolt_support_lenght_2=105.15 mm; Bottom_profile=37.58 mm; D1=105.5 mm; DN=150.3 mm; FOD=142.5 mm; Fillet_Length=8 mm  [stored 0.0262467 ft]; H3=525 mm; ID=75.15 mm; L=480 mm; L1=497 mm; L_Ref=488.5 mm; L_ref_2=221 mm; PG_Dia=80 mm; PG_Ref=80 mm; PG_depth=11.2 mm  [stored 0.0367454 ft]; PG_ref=85.15 mm; Pilot_Dia_1=31 mm; Pilot_Dia_1_Ref=37.2 mm; Pilot_Dia_1_Ref_2=74.4 mm; Pilot_Dia_2=77.5 mm; Pilot_Dia_3=20.67 mm; Pilot_Dia_4=10.33 mm; Pilot_Dia_5=6.89 mm; Pilot_top_1=332.75 mm; Pilot_top_ref=49.75 mm; Profile1_Height=230 mm; Profile1_Length=38.51 mm; Profile1_Length_2=25.68 mm; Profile_Dia=8 mm  [stored 0.0262467 ft]; Profile_Dia_2=8 mm  [stored 0.0262467 ft]; Profile_Dia_3=16 mm  [stored 0.0524934 ft]; Top_Profile=169.41 mm; Top_Profile_Ref=174.41 mm; Top_Ref=283 mm; Top_Ref_2=307.88 mm; W=340 mm; W_Ref=262.5 mm
- 879-0150-00-14400227299_DN150_PN10/16: A=124 mm; Body_Collar_Dia=50 mm; Body_Collar_Dia_2=24 mm; Body_Flange_Dia=126.32 mm; Body_Flange_Dia_2=129.73 mm; Body_Height_1=120 mm; Body_Height_2=60 mm; Body_Height_3=60 mm; Body_Height_4=75 mm; Body_Top_Dia=15 mm  [stored 0.0492126 ft]; Body_Top_Dia_2=12.5 mm  [stored 0.0410105 ft]; Body_With_Dia=106.67 mm; Body_With_Dia_2=106.67 mm; Bolt_support=282.35 mm; Bolt_support_2=141.18 mm; Bolt_support_Dia=16 mm  [stored 0.0524934 ft]; Bolt_support_lenght=95.2 mm; Bolt_support_lenght_2=105.2 mm; Bottom_profile=37.6 mm; D1=105.5 mm; DN=150.4 mm; FOD=142.5 mm; Fillet_Length=8 mm  [stored 0.0262467 ft]; H3=525 mm; ID=75.2 mm; L=480 mm; L1=497 mm; L_Ref=488.5 mm; L_ref_2=221 mm; PG_Dia=80 mm; PG_Ref=80 mm; PG_depth=11.2 mm  [stored 0.0367454 ft]; PG_ref=85.2 mm; Pilot_Dia_1=31 mm; Pilot_Dia_1_Ref=37.2 mm; Pilot_Dia_1_Ref_2=74.4 mm; Pilot_Dia_2=77.5 mm; Pilot_Dia_3=20.67 mm; Pilot_Dia_4=10.33 mm; Pilot_Dia_5=6.89 mm; Pilot_top_1=328.75 mm; Pilot_top_ref=53.75 mm; Profile1_Height=230 mm; Profile1_Length=38.51 mm; Profile1_Length_2=25.68 mm; Profile_Dia=8 mm  [stored 0.0262467 ft]; Profile_Dia_2=8 mm  [stored 0.0262467 ft]; Profile_Dia_3=16 mm  [stored 0.0524934 ft]; Top_Profile=169.41 mm; Top_Profile_Ref=174.41 mm; Top_Ref=275 mm; Top_Ref_2=301.88 mm; W=340 mm; W_Ref=262.5 mm
- 879-0150-00-144002272A0_DN150_PN10/16: A=124 mm; Body_Collar_Dia=50 mm; Body_Collar_Dia_2=24 mm; Body_Flange_Dia=126.32 mm; Body_Flange_Dia_2=129.73 mm; Body_Height_1=120 mm; Body_Height_2=60 mm; Body_Height_3=68 mm; Body_Height_4=75 mm; Body_Top_Dia=15 mm  [stored 0.0492126 ft]; Body_Top_Dia_2=12.5 mm  [stored 0.0410105 ft]; Body_With_Dia=106.67 mm; Body_With_Dia_2=106.67 mm; Bolt_support=282.35 mm; Bolt_support_2=141.18 mm; Bolt_support_Dia=16 mm  [stored 0.0524934 ft]; Bolt_support_lenght=95.25 mm; Bolt_support_lenght_2=105.25 mm; Bottom_profile=37.63 mm; D1=105.5 mm; DN=150.5 mm; FOD=142.5 mm; Fillet_Length=8 mm  [stored 0.0262467 ft]; H3=525 mm; ID=75.25 mm; L=480 mm; L1=497 mm; L_Ref=488.5 mm; L_ref_2=221 mm; PG_Dia=80 mm; PG_Ref=80 mm; PG_depth=11.2 mm  [stored 0.0367454 ft]; PG_ref=85.25 mm; Pilot_Dia_1=31 mm; Pilot_Dia_1_Ref=37.2 mm; Pilot_Dia_1_Ref_2=74.4 mm; Pilot_Dia_2=77.5 mm; Pilot_Dia_3=20.67 mm; Pilot_Dia_4=10.33 mm; Pilot_Dia_5=6.89 mm; Pilot_top_1=332.75 mm; Pilot_top_ref=49.75 mm; Profile1_Height=230 mm; Profile1_Length=38.51 mm; Profile1_Length_2=25.68 mm; Profile_Dia=8 mm  [stored 0.0262467 ft]; Profile_Dia_2=8 mm  [stored 0.0262467 ft]; Profile_Dia_3=16 mm  [stored 0.0524934 ft]; Top_Profile=169.41 mm; Top_Profile_Ref=174.41 mm; Top_Ref=283 mm; Top_Ref_2=307.88 mm; W=340 mm; W_Ref=262.5 mm
- 879-0150-00-14400237299_DN150_PN10/16: A=124 mm; Body_Collar_Dia=50 mm; Body_Collar_Dia_2=24 mm; Body_Flange_Dia=126.32 mm; Body_Flange_Dia_2=129.73 mm; Body_Height_1=120 mm; Body_Height_2=60 mm; Body_Height_3=60 mm; Body_Height_4=75 mm; Body_Top_Dia=15 mm  [stored 0.0492126 ft]; Body_Top_Dia_2=12.5 mm  [stored 0.0410105 ft]; Body_With_Dia=106.67 mm; Body_With_Dia_2=106.67 mm; Bolt_support=282.35 mm; Bolt_support_2=141.18 mm; Bolt_support_Dia=16 mm  [stored 0.0524934 ft]; Bolt_support_lenght=95.3 mm; Bolt_support_lenght_2=105.3 mm; Bottom_profile=37.65 mm; D1=105.5 mm; DN=150.6 mm; FOD=142.5 mm; Fillet_Length=8 mm  [stored 0.0262467 ft]; H3=525 mm; ID=75.3 mm; L=480 mm; L1=497 mm; L_Ref=488.5 mm; L_ref_2=221 mm; PG_Dia=80 mm; PG_Ref=80 mm; PG_depth=11.2 mm  [stored 0.0367454 ft]; PG_ref=85.3 mm; Pilot_Dia_1=31 mm; Pilot_Dia_1_Ref=37.2 mm; Pilot_Dia_1_Ref_2=74.4 mm; Pilot_Dia_2=77.5 mm; Pilot_Dia_3=20.67 mm; Pilot_Dia_4=10.33 mm; Pilot_Dia_5=6.89 mm; Pilot_top_1=328.75 mm; Pilot_top_ref=53.75 mm; Profile1_Height=230 mm; Profile1_Length=38.51 mm; Profile1_Length_2=25.68 mm; Profile_Dia=8 mm  [stored 0.0262467 ft]; Profile_Dia_2=8 mm  [stored 0.0262467 ft]; Profile_Dia_3=16 mm  [stored 0.0524934 ft]; Top_Profile=169.41 mm; Top_Profile_Ref=174.41 mm; Top_Ref=275 mm; Top_Ref_2=301.88 mm; W=340 mm; W_Ref=262.5 mm
- 879-0150-00-144002372A0_DN150_PN10/16: A=124 mm; Body_Collar_Dia=50 mm; Body_Collar_Dia_2=24 mm; Body_Flange_Dia=126.32 mm; Body_Flange_Dia_2=129.73 mm; Body_Height_1=120 mm; Body_Height_2=60 mm; Body_Height_3=68 mm; Body_Height_4=75 mm; Body_Top_Dia=15 mm  [stored 0.0492126 ft]; Body_Top_Dia_2=12.5 mm  [stored 0.0410105 ft]; Body_With_Dia=106.67 mm; Body_With_Dia_2=106.67 mm; Bolt_support=282.35 mm; Bolt_support_2=141.18 mm; Bolt_support_Dia=16 mm  [stored 0.0524934 ft]; Bolt_support_lenght=95.35 mm; Bolt_support_lenght_2=105.35 mm; Bottom_profile=37.68 mm; D1=105.5 mm; DN=150.7 mm; FOD=142.5 mm; Fillet_Length=8 mm  [stored 0.0262467 ft]; H3=525 mm; ID=75.35 mm; L=480 mm; L1=497 mm; L_Ref=488.5 mm; L_ref_2=221 mm; PG_Dia=80 mm; PG_Ref=80 mm; PG_depth=11.2 mm  [stored 0.0367454 ft]; PG_ref=85.35 mm; Pilot_Dia_1=31 mm; Pilot_Dia_1_Ref=37.2 mm; Pilot_Dia_1_Ref_2=74.4 mm; Pilot_Dia_2=77.5 mm; Pilot_Dia_3=20.67 mm; Pilot_Dia_4=10.33 mm; Pilot_Dia_5=6.89 mm; Pilot_top_1=332.75 mm; Pilot_top_ref=49.75 mm; Profile1_Height=230 mm; Profile1_Length=38.51 mm; Profile1_Length_2=25.68 mm; Profile_Dia=8 mm  [stored 0.0262467 ft]; Profile_Dia_2=8 mm  [stored 0.0262467 ft]; Profile_Dia_3=16 mm  [stored 0.0524934 ft]; Top_Profile=169.41 mm; Top_Profile_Ref=174.41 mm; Top_Ref=283 mm; Top_Ref_2=307.88 mm; W=340 mm; W_Ref=262.5 mm
- 879-0080-00-14400207299_DN80_PN10/16: A=124.25 mm; Body_Collar_Dia=32.29 mm; Body_Collar_Dia_2=15.5 mm  [stored 0.050853 ft]; Body_Flange_Dia=81.58 mm; Body_Flange_Dia_2=83.78 mm; Body_Height_1=77.5 mm; Body_Height_2=38.75 mm; Body_Height_3=62 mm; Body_Height_4=53.75 mm; Body_Top_Dia=9.69 mm; Body_Top_Dia_2=8.07 mm; Body_With_Dia=68.89 mm; Body_With_Dia_2=68.89 mm; Bolt_support=182.35 mm; Bolt_support_2=91.18 mm; Bolt_support_Dia=12 mm  [stored 0.0393701 ft]; Bolt_support_lenght=60 mm; Bolt_support_lenght_2=70 mm; Bottom_profile=20 mm; D1=66 mm; DN=80 mm; FOD=100 mm; Fillet_Length=6 mm  [stored 0.019685 ft]; H3=500 mm; ID=40 mm; L=310 mm; L1=327 mm; L_Ref=318.5 mm; L_ref_2=136 mm; PG_Dia=40 mm; PG_Ref=51.67 mm; PG_depth=8.4 mm  [stored 0.0275591 ft]; PG_ref=50 mm; Pilot_Dia_1=19.5 mm; Pilot_Dia_1_Ref=23.4 mm; Pilot_Dia_1_Ref_2=46.8 mm; Pilot_Dia_2=48.75 mm; Pilot_Dia_3=13 mm; Pilot_Dia_4=6.5 mm; Pilot_Dia_5=4.33 mm; Pilot_top_1=306.63 mm; Pilot_top_ref=93.38 mm; Profile1_Height=179 mm; Profile1_Length=27.03 mm; Profile1_Length_2=18.02 mm; Profile_Dia=6 mm  [stored 0.019685 ft]; Profile_Dia_2=6 mm  [stored 0.019685 ft]; Profile_Dia_3=12 mm  [stored 0.0393701 ft]; Top_Profile=109.41 mm; Top_Profile_Ref=114.41 mm; Top_Ref=213.25 mm; Top_Ref_2=259.94 mm; W=270 mm; W_Ref=221.25 mm
- 879-0080-00-144002072A0_DN80_PN10/16: A=124.25 mm; Body_Collar_Dia=32.29 mm; Body_Collar_Dia_2=15.5 mm  [stored 0.050853 ft]; Body_Flange_Dia=81.58 mm; Body_Flange_Dia_2=83.78 mm; Body_Height_1=77.5 mm; Body_Height_2=38.75 mm; Body_Height_3=77.5 mm; Body_Height_4=53.75 mm; Body_Top_Dia=9.69 mm; Body_Top_Dia_2=8.07 mm; Body_With_Dia=68.89 mm; Body_With_Dia_2=68.89 mm; Bolt_support=182.35 mm; Bolt_support_2=91.18 mm; Bolt_support_Dia=12 mm  [stored 0.0393701 ft]; Bolt_support_lenght=60.05 mm; Bolt_support_lenght_2=70.05 mm; Bottom_profile=20.03 mm; D1=66 mm; DN=80.1 mm; FOD=100 mm; Fillet_Length=6 mm  [stored 0.019685 ft]; H3=500 mm; ID=40.05 mm; L=310 mm; L1=327 mm; L_Ref=318.5 mm; L_ref_2=136 mm; PG_Dia=40 mm; PG_Ref=51.67 mm; PG_depth=8.4 mm  [stored 0.0275591 ft]; PG_ref=50.05 mm; Pilot_Dia_1=19.5 mm; Pilot_Dia_1_Ref=23.4 mm; Pilot_Dia_1_Ref_2=46.8 mm; Pilot_Dia_2=48.75 mm; Pilot_Dia_3=13 mm; Pilot_Dia_4=6.5 mm; Pilot_Dia_5=4.33 mm; Pilot_top_1=314.38 mm; Pilot_top_ref=85.63 mm; Profile1_Height=168 mm; Profile1_Length=27.03 mm; Profile1_Length_2=18.02 mm; Profile_Dia=6 mm  [stored 0.019685 ft]; Profile_Dia_2=6 mm  [stored 0.019685 ft]; Profile_Dia_3=12 mm  [stored 0.0393701 ft]; Top_Profile=109.41 mm; Top_Profile_Ref=114.41 mm; Top_Ref=228.75 mm; Top_Ref_2=271.56 mm; W=270 mm; W_Ref=221.25 mm
- 879-0080-00-14400217299_DN80_PN10/16: A=124.25 mm; Body_Collar_Dia=32.29 mm; Body_Collar_Dia_2=15.5 mm  [stored 0.050853 ft]; Body_Flange_Dia=81.58 mm; Body_Flange_Dia_2=83.78 mm; Body_Height_1=77.5 mm; Body_Height_2=38.75 mm; Body_Height_3=62 mm; Body_Height_4=53.75 mm; Body_Top_Dia=9.69 mm; Body_Top_Dia_2=8.07 mm; Body_With_Dia=68.89 mm; Body_With_Dia_2=68.89 mm; Bolt_support=182.35 mm; Bolt_support_2=91.18 mm; Bolt_support_Dia=12 mm  [stored 0.0393701 ft]; Bolt_support_lenght=60.1 mm; Bolt_support_lenght_2=70.1 mm; Bottom_profile=20.05 mm; D1=66 mm; DN=80.2 mm; FOD=100 mm; Fillet_Length=6 mm  [stored 0.019685 ft]; H3=500 mm; ID=40.1 mm; L=310 mm; L1=327 mm; L_Ref=318.5 mm; L_ref_2=136 mm; PG_Dia=40 mm; PG_Ref=51.67 mm; PG_depth=8.4 mm  [stored 0.0275591 ft]; PG_ref=50.1 mm; Pilot_Dia_1=19.5 mm; Pilot_Dia_1_Ref=23.4 mm; Pilot_Dia_1_Ref_2=46.8 mm; Pilot_Dia_2=48.75 mm; Pilot_Dia_3=13 mm; Pilot_Dia_4=6.5 mm; Pilot_Dia_5=4.33 mm; Pilot_top_1=306.63 mm; Pilot_top_ref=93.38 mm; Profile1_Height=179 mm; Profile1_Length=27.03 mm; Profile1_Length_2=18.02 mm; Profile_Dia=6 mm  [stored 0.019685 ft]; Profile_Dia_2=6 mm  [stored 0.019685 ft]; Profile_Dia_3=12 mm  [stored 0.0393701 ft]; Top_Profile=109.41 mm; Top_Profile_Ref=114.41 mm; Top_Ref=213.25 mm; Top_Ref_2=259.94 mm; W=270 mm; W_Ref=221.25 mm
- 879-0080-00-144002172A0_DN80_PN10/16: A=124.25 mm; Body_Collar_Dia=32.29 mm; Body_Collar_Dia_2=15.5 mm  [stored 0.050853 ft]; Body_Flange_Dia=81.58 mm; Body_Flange_Dia_2=83.78 mm; Body_Height_1=77.5 mm; Body_Height_2=38.75 mm; Body_Height_3=77.5 mm; Body_Height_4=53.75 mm; Body_Top_Dia=9.69 mm; Body_Top_Dia_2=8.07 mm; Body_With_Dia=68.89 mm; Body_With_Dia_2=68.89 mm; Bolt_support=182.35 mm; Bolt_support_2=91.18 mm; Bolt_support_Dia=12 mm  [stored 0.0393701 ft]; Bolt_support_lenght=60.15 mm; Bolt_support_lenght_2=70.15 mm; Bottom_profile=20.08 mm; D1=66 mm; DN=80.3 mm; FOD=100 mm; Fillet_Length=6 mm  [stored 0.019685 ft]; H3=500 mm; ID=40.15 mm; L=310 mm; L1=327 mm; L_Ref=318.5 mm; L_ref_2=136 mm; PG_Dia=40 mm; PG_Ref=51.67 mm; PG_depth=8.4 mm  [stored 0.0275591 ft]; PG_ref=50.15 mm; Pilot_Dia_1=19.5 mm; Pilot_Dia_1_Ref=23.4 mm; Pilot_Dia_1_Ref_2=46.8 mm; Pilot_Dia_2=48.75 mm; Pilot_Dia_3=13 mm; Pilot_Dia_4=6.5 mm; Pilot_Dia_5=4.33 mm; Pilot_top_1=314.38 mm; Pilot_top_ref=85.63 mm; Profile1_Height=168 mm; Profile1_Length=27.03 mm; Profile1_Length_2=18.02 mm; Profile_Dia=6 mm  [stored 0.019685 ft]; Profile_Dia_2=6 mm  [stored 0.019685 ft]; Profile_Dia_3=12 mm  [stored 0.0393701 ft]; Top_Profile=109.41 mm; Top_Profile_Ref=114.41 mm; Top_Ref=228.75 mm; Top_Ref_2=271.56 mm; W=270 mm; W_Ref=221.25 mm
- 879-0080-00-14400227299_DN80_PN10/16: A=124.25 mm; Body_Collar_Dia=32.29 mm; Body_Collar_Dia_2=15.5 mm  [stored 0.050853 ft]; Body_Flange_Dia=81.58 mm; Body_Flange_Dia_2=83.78 mm; Body_Height_1=77.5 mm; Body_Height_2=38.75 mm; Body_Height_3=62 mm; Body_Height_4=53.75 mm; Body_Top_Dia=9.69 mm; Body_Top_Dia_2=8.07 mm; Body_With_Dia=68.89 mm; Body_With_Dia_2=68.89 mm; Bolt_support=182.35 mm; Bolt_support_2=91.18 mm; Bolt_support_Dia=12 mm  [stored 0.0393701 ft]; Bolt_support_lenght=60.2 mm; Bolt_support_lenght_2=70.2 mm; Bottom_profile=20.1 mm; D1=66 mm; DN=80.4 mm; FOD=100 mm; Fillet_Length=6 mm  [stored 0.019685 ft]; H3=500 mm; ID=40.2 mm; L=310 mm; L1=327 mm; L_Ref=318.5 mm; L_ref_2=136 mm; PG_Dia=40 mm; PG_Ref=51.67 mm; PG_depth=8.4 mm  [stored 0.0275591 ft]; PG_ref=50.2 mm; Pilot_Dia_1=19.5 mm; Pilot_Dia_1_Ref=23.4 mm; Pilot_Dia_1_Ref_2=46.8 mm; Pilot_Dia_2=48.75 mm; Pilot_Dia_3=13 mm; Pilot_Dia_4=6.5 mm; Pilot_Dia_5=4.33 mm; Pilot_top_1=306.63 mm; Pilot_top_ref=93.38 mm; Profile1_Height=179 mm; Profile1_Length=27.03 mm; Profile1_Length_2=18.02 mm; Profile_Dia=6 mm  [stored 0.019685 ft]; Profile_Dia_2=6 mm  [stored 0.019685 ft]; Profile_Dia_3=12 mm  [stored 0.0393701 ft]; Top_Profile=109.41 mm; Top_Profile_Ref=114.41 mm; Top_Ref=213.25 mm; Top_Ref_2=259.94 mm; W=270 mm; W_Ref=221.25 mm
- 879-0080-00-144002272A0_DN80_PN10/16: A=124.25 mm; Body_Collar_Dia=32.29 mm; Body_Collar_Dia_2=15.5 mm  [stored 0.050853 ft]; Body_Flange_Dia=81.58 mm; Body_Flange_Dia_2=83.78 mm; Body_Height_1=77.5 mm; Body_Height_2=38.75 mm; Body_Height_3=77.5 mm; Body_Height_4=53.75 mm; Body_Top_Dia=9.69 mm; Body_Top_Dia_2=8.07 mm; Body_With_Dia=68.89 mm; Body_With_Dia_2=68.89 mm; Bolt_support=182.35 mm; Bolt_support_2=91.18 mm; Bolt_support_Dia=12 mm  [stored 0.0393701 ft]; Bolt_support_lenght=60.25 mm; Bolt_support_lenght_2=70.25 mm; Bottom_profile=20.13 mm; D1=66 mm; DN=80.5 mm; FOD=100 mm; Fillet_Length=6 mm  [stored 0.019685 ft]; H3=500 mm; ID=40.25 mm; L=310 mm; L1=327 mm; L_Ref=318.5 mm; L_ref_2=136 mm; PG_Dia=40 mm; PG_Ref=51.67 mm; PG_depth=8.4 mm  [stored 0.0275591 ft]; PG_ref=50.25 mm; Pilot_Dia_1=19.5 mm; Pilot_Dia_1_Ref=23.4 mm; Pilot_Dia_1_Ref_2=46.8 mm; Pilot_Dia_2=48.75 mm; Pilot_Dia_3=13 mm; Pilot_Dia_4=6.5 mm; Pilot_Dia_5=4.33 mm; Pilot_top_1=314.38 mm; Pilot_top_ref=85.63 mm; Profile1_Height=168 mm; Profile1_Length=27.03 mm; Profile1_Length_2=18.02 mm; Profile_Dia=6 mm  [stored 0.019685 ft]; Profile_Dia_2=6 mm  [stored 0.019685 ft]; Profile_Dia_3=12 mm  [stored 0.0393701 ft]; Top_Profile=109.41 mm; Top_Profile_Ref=114.41 mm; Top_Ref=228.75 mm; Top_Ref_2=271.56 mm; W=270 mm; W_Ref=221.25 mm

note: [stored X ft] marks values corroborated as IEEE doubles in the binary element streams (Revit-internal decimal feet)

## geometry (parser evidence)
native form markers: Sweep x4
no freeform markers — native parametric forms only
